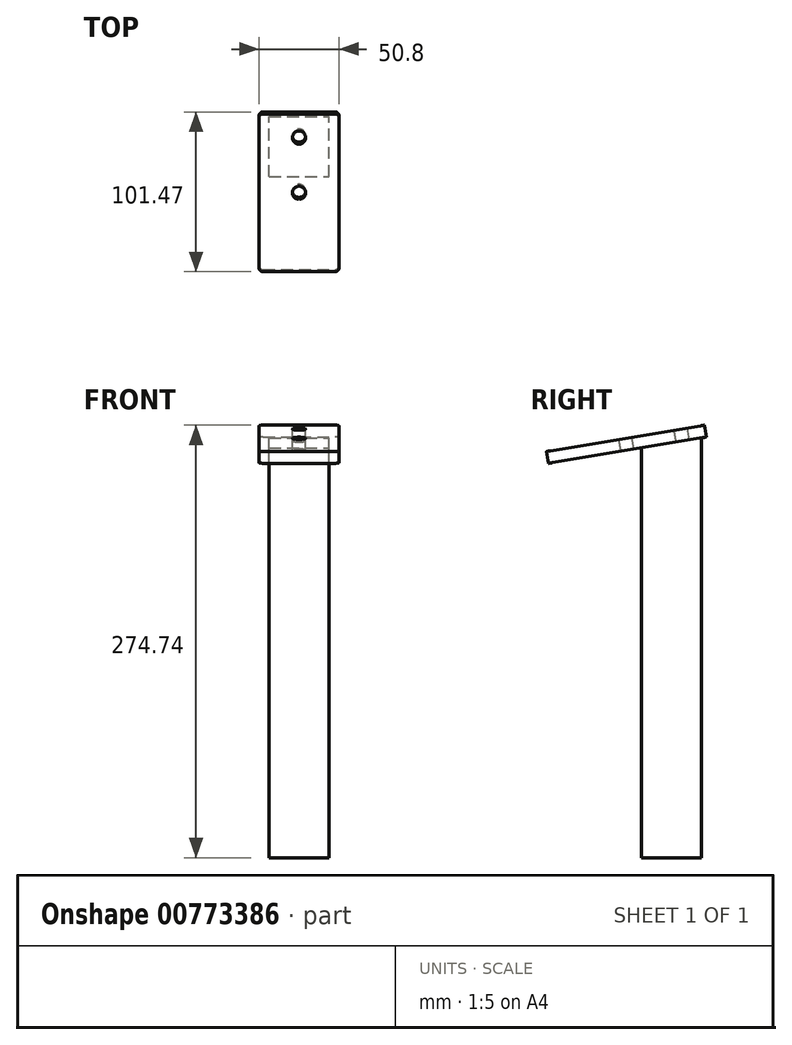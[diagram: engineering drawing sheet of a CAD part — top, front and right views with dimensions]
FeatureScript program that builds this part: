
annotation { "Feature Type Name" : "Feature", "Feature Type Description" : "" }
export const myFeature = defineFeature(function(context is Context, id is Id, definition is map)
    precondition{}
    {
        {
            var Q0;
            Q0=qCreatedBy(makeId("Front.planeOp"),FACE);
            var sketch = newSketch(context, id + "F0", { "sketchPlane" : qUnion([Q0])});
            skLineSegment(sketch, "E0.bottom", {"start": v(0, 0) * mm, "end": v(38.1, 0) * mm});
            skLineSegment(sketch, "E0.top", {"start": v(0, 260.35) * mm, "end": v(38.1, 260.35) * mm});
            skLineSegment(sketch, "E0.left", {"start": v(0, 0) * mm, "end": v(0, 260.35) * mm});
            skLineSegment(sketch, "E0.right", {"start": v(38.1, 0) * mm, "end": v(38.1, 260.35) * mm});
            skSolve(sketch);
        }
        {
            var Q0;
            Q0=qCreatedBy(makeId("Front.planeOp"),FACE);
            cPlane(context, id + "F1", {"entities" : qUnion([Q0]), "cplaneType" : CPlaneType.OFFSET, "offset" : 38.1 * mm, "oppositeDirection" : true, "width" : 152.4 * mm, "height" : 152.4 * mm});
        }
        {
            var Q0;
            Q0=qCreatedBy(id+"F1.planeOp",FACE);
            var sketch = newSketch(context, id + "F2", { "sketchPlane" : qUnion([Q0])});
            skLineSegment(sketch, "E1.bottom", {"start": v(0, 0) * mm, "end": v(38.1, 0) * mm});
            skLineSegment(sketch, "E1.top", {"start": v(0, 266.7) * mm, "end": v(38.1, 266.7) * mm});
            skLineSegment(sketch, "E1.left", {"start": v(0, 0) * mm, "end": v(0, 266.7) * mm});
            skLineSegment(sketch, "E1.right", {"start": v(38.1, 0) * mm, "end": v(38.1, 266.7) * mm});
            skSolve(sketch);
        }
        {
            var Q0;
            Q0=makeQuery(id+"F0.imprint","IMPRINT",FACE,{"disambiguationData":[TD([[makeQuery(id+"F0.imprint","IMPRINT",EDGE,{"derivedFrom":sQuery(id+"F0.wireOp",EDGE,"E0.bottom")}),1.0]])]});
            var Q1;
            Q1=makeQuery(id+"F2.imprint","IMPRINT",FACE,{"disambiguationData":[TD([[makeQuery(id+"F2.imprint","IMPRINT",EDGE,{"derivedFrom":sQuery(id+"F2.wireOp",EDGE,"E1.bottom")}),1.0]])]});
            loft(context, id + "F3", {"sheetProfilesArray" : [{ "sheetProfileEntities" : qUnion([Q0]) }, { "sheetProfileEntities" : qUnion([Q1]) }]});
        }
        {
            var Q0;
            Q0=makeQuery(id+"F3.opLoft","SWEPT_FACE",FACE,{"disambiguationData":[OSD([sQuery(id+"F0.wireOp",EDGE,"E0.top"),sQuery(id+"F0.wireOp",EDGE,"E0.left"),sQuery(id+"F0.wireOp",EDGE,"E0.right"),sQuery(id+"F2.wireOp",EDGE,"E1.top"),sQuery(id+"F2.wireOp",EDGE,"E1.left"),sQuery(id+"F2.wireOp",EDGE,"E1.right")])]});
            var sketch = newSketch(context, id + "F4", { "sketchPlane" : qUnion([Q0])});
            skLineSegment(sketch, "E2.left", {"start": v(-6.35, 81.43) * mm, "end": v(-6.35, 81.43) * mm});
            skLineSegment(sketch, "E2.right", {"start": v(0, 81.43) * mm, "end": v(0, 81.43) * mm});
            skLineSegment(sketch, "E3", {"start": v(-6.35, 84.6) * mm, "end": v(-6.35, 81.43) * mm});
            skLineSegment(sketch, "E4.bottom", {"start": v(-6.35, 84.6) * mm, "end": v(44.45, 84.6) * mm});
            skLineSegment(sketch, "E4.top", {"start": v(-6.35, -17) * mm, "end": v(44.45, -17) * mm});
            skLineSegment(sketch, "E4.left", {"start": v(-6.35, 84.6) * mm, "end": v(-6.35, -17) * mm});
            skLineSegment(sketch, "E4.right", {"start": v(44.45, 84.6) * mm, "end": v(44.45, -17) * mm});
            skSolve(sketch);
        }
        {
            var Q0;
            {var subQ1=sQuery(id+"F4.wireOp",EDGE,"E4.bottom");Q0=makeQuery(id+"F4.imprint","IMPRINT",FACE,{"disambiguationData":[TD([[makeQuery(id+"F4.imprint","IMPRINT",EDGE,{"derivedFrom":subQ1}),-1.0]])]});}
            var Q1;
            {var subQ0=sQuery(id+"F0.wireOp",EDGE,"E0.right");var subQ1=sQuery(id+"F0.wireOp",EDGE,"E0.left");var subQ2=sQuery(id+"F0.wireOp",EDGE,"E0.top");Q1=makeQuery(id+"F4.imprint","IMPRINT",FACE,{"disambiguationData":[TD([[makeQuery(id+"F4.imprint","IMPRINT",EDGE,{"derivedFrom":makeQuery(id+"F3.opLoft","MID_CAP_EDGE",EDGE,{"disambiguationData":[OSD([subQ2,subQ1,subQ0])],"capPos":0.0})}),1.0]])]});}
            extrude(context, id + "F5", {"entities" : qUnion([Q0, Q1]), "depth" : 7.62 * mm, "offsetDistance" : 25.4 * mm});
        }
        {
            var Q0;
            Q0=makeQuery(id+"F5.opExtrude","CAP_FACE",FACE,{"disambiguationData":[OSD([sQuery(id+"F4.wireOp",EDGE,"E4.bottom"),sQuery(id+"F4.wireOp",EDGE,"E4.top"),sQuery(id+"F4.wireOp",EDGE,"E4.left"),sQuery(id+"F4.wireOp",EDGE,"E4.right")])],"isStart":false});
            var sketch = newSketch(context, id + "F6", { "sketchPlane" : qUnion([Q0])});
            skCircle(sketch, "E5", {"center": v(19.05, 69.36) * mm, "radius": 4.23 * mm});
            skCircle(sketch, "E6", {"center": v(19.05, 33.8) * mm, "radius": 4.23 * mm});
            skSolve(sketch);
        }
        {
            var Q0;
            Q0=makeQuery(id+"F6.imprint","IMPRINT",FACE,{"disambiguationData":[TD([[makeQuery(id+"F6.imprint","IMPRINT",EDGE,{"derivedFrom":sQuery(id+"F6.wireOp",EDGE,"E6")}),1.0]])]});
            var Q1;
            Q1=makeQuery(id+"F6.imprint","IMPRINT",FACE,{"disambiguationData":[TD([[makeQuery(id+"F6.imprint","IMPRINT",EDGE,{"derivedFrom":sQuery(id+"F6.wireOp",EDGE,"E5")}),1.0]])]});
            extrude(context, id + "F7", {"entities" : qUnion([Q0, Q1]), "operationType" : NewBodyOperationType.REMOVE, "oppositeDirection" : true, "depth" : 7.62 * mm, "offsetDistance" : 25.4 * mm});
        }
        {
            var Q0;
            Q0=makeQuery(id+"F5.opExtrude","SWEPT_EDGE",EDGE,{"disambiguationData":[OSD([sQuery(id+"F4.wireOp",EDGE,"E4.top"),sQuery(id+"F4.wireOp",EDGE,"E4.right")])]});
            var Q1;
            Q1=makeQuery(id+"F5.opExtrude","SWEPT_EDGE",EDGE,{"disambiguationData":[OSD([sQuery(id+"F4.wireOp",EDGE,"E4.top"),sQuery(id+"F4.wireOp",EDGE,"E4.left")])]});
            var Q2;
            Q2=makeQuery(id+"F5.opExtrude","SWEPT_EDGE",EDGE,{"disambiguationData":[OSD([sQuery(id+"F4.wireOp",EDGE,"E4.bottom"),sQuery(id+"F4.wireOp",EDGE,"E4.left")])]});
            var Q3;
            Q3=makeQuery(id+"F5.opExtrude","SWEPT_EDGE",EDGE,{"disambiguationData":[OSD([sQuery(id+"F4.wireOp",EDGE,"E4.bottom"),sQuery(id+"F4.wireOp",EDGE,"E4.right")])]});
            fillet(context, id + "F8", {"entities" : qUnion([Q0, Q1, Q2, Q3]), "radius" : 2.54 * mm, "tangentPropagation" : true, "allowEdgeOverflow" : false});
        }
    });
